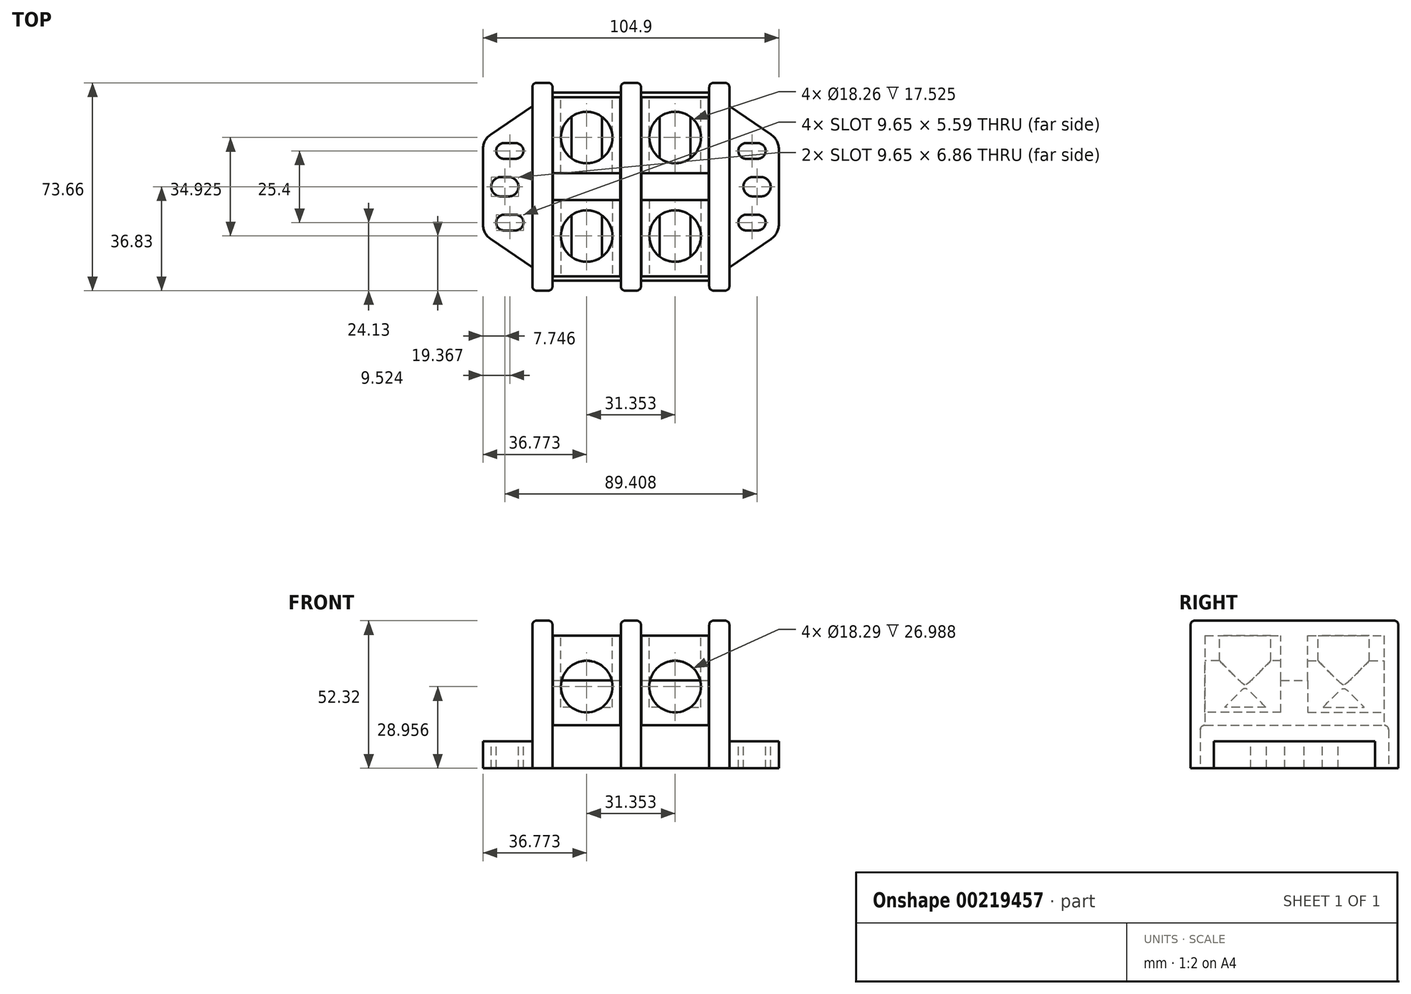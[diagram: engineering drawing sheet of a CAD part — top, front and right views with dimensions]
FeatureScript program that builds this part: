
annotation { "Feature Type Name" : "Feature", "Feature Type Description" : "" }
export const myFeature = defineFeature(function(context is Context, id is Id, definition is map)
    precondition{}
    {
        {
            var Q0;
            Q0=qCreatedBy(makeId("Top.planeOp"),FACE);
            var sketch = newSketch(context, id + "F0", { "sketchPlane" : qUnion([Q0])});
            skLineSegment(sketch, "E0.bottom", {"start": v(-3.57, -36.83) * mm, "end": v(3.57, -36.83) * mm});
            skLineSegment(sketch, "E0.top", {"start": v(-3.57, 36.83) * mm, "end": v(3.57, 36.83) * mm});
            skLineSegment(sketch, "E0.left", {"start": v(-3.57, -36.83) * mm, "end": v(-3.57, 36.83) * mm});
            skLineSegment(sketch, "E0.right", {"start": v(3.57, -36.83) * mm, "end": v(3.57, 36.83) * mm});
            skPoint(sketch, "E0.middle", {"position": v(0, 0) * mm});
            skLineSegment(sketch, "E1.bottom", {"start": v(-27.78, -36.83) * mm, "end": v(-34.93, -36.83) * mm});
            skLineSegment(sketch, "E1.top", {"start": v(-27.78, 36.83) * mm, "end": v(-34.93, 36.83) * mm});
            skLineSegment(sketch, "E1.left", {"start": v(-27.78, -36.83) * mm, "end": v(-27.78, 36.83) * mm});
            skLineSegment(sketch, "E1.right", {"start": v(-34.93, -36.83) * mm, "end": v(-34.93, 36.83) * mm});
            skPoint(sketch, "E1.middle", {"position": v(-31.35, 0) * mm});
            skLineSegment(sketch, "E2.bottom", {"start": v(27.78, -36.83) * mm, "end": v(34.93, -36.83) * mm});
            skLineSegment(sketch, "E2.top", {"start": v(27.78, 36.83) * mm, "end": v(34.93, 36.83) * mm});
            skLineSegment(sketch, "E2.left", {"start": v(27.78, -36.83) * mm, "end": v(27.78, 36.83) * mm});
            skLineSegment(sketch, "E2.right", {"start": v(34.93, -36.83) * mm, "end": v(34.93, 36.83) * mm});
            skPoint(sketch, "E2.middle", {"position": v(31.35, 0) * mm});
            skSolve(sketch);
        }
        {
            var Q0;
            Q0=qSketchRegion(id+"F0",true);
            extrude(context, id + "F1", {"entities" : qUnion([Q0]), "depth" : 52.32 * mm});
        }
        {
            var Q0;
            Q0=qCreatedBy(makeId("Top.planeOp"),FACE);
            var sketch = newSketch(context, id + "F2", { "sketchPlane" : qUnion([Q0])});
            skLineSegment(sketch, "E3.bottom", {"start": v(-27.78, -33.34) * mm, "end": v(27.78, -33.34) * mm});
            skLineSegment(sketch, "E3.top", {"start": v(-27.78, 33.34) * mm, "end": v(27.78, 33.34) * mm});
            skLineSegment(sketch, "E3.left", {"start": v(-27.78, -33.34) * mm, "end": v(-27.78, 33.34) * mm});
            skLineSegment(sketch, "E3.right", {"start": v(27.78, -33.34) * mm, "end": v(27.78, 33.34) * mm});
            skPoint(sketch, "E3.middle", {"position": v(0, 0) * mm});
            skSolve(sketch);
        }
        {
            var Q0;
            Q0=qSketchRegion(id+"F2",true);
            extrude(context, id + "F3", {"entities" : qUnion([Q0]), "depth" : 15.24 * mm});
        }
        {
            var Q0;
            Q0=qCreatedBy(makeId("Top.planeOp"),FACE);
            var sketch = newSketch(context, id + "F4", { "sketchPlane" : qUnion([Q0])});
            skLineSegment(sketch, "E4", {"start": v(-34.93, 28.58) * mm, "end": v(-52.45, 16.67) * mm});
            skLineSegment(sketch, "E5", {"start": v(-52.45, 16.67) * mm, "end": v(-52.45, -16.67) * mm});
            skLineSegment(sketch, "E6", {"start": v(-52.45, -16.67) * mm, "end": v(-34.93, -28.58) * mm});
            skLineSegment(sketch, "E7", {"start": v(-34.93, -28.58) * mm, "end": v(-34.93, 28.58) * mm});
            skSolve(sketch);
        }
        {
            var Q0;
            Q0=qSketchRegion(id+"F4",true);
            extrude(context, id + "F5", {"entities" : qUnion([Q0]), "operationType" : NewBodyOperationType.ADD, "depth" : 9.52 * mm});
        }
        {
            var Q0;
            Q0=makeQuery(id+"F1.opExtrude","SWEPT_EDGE",EDGE,{"disambiguationData":[OSD([sQuery(id+"F0.wireOp",EDGE,"E1.top"),sQuery(id+"F0.wireOp",EDGE,"E1.right")])]});
            var Q1;
            Q1=makeQuery(id+"F1.opExtrude","CAP_EDGE",EDGE,{"disambiguationData":[OSD([sQuery(id+"F0.wireOp",EDGE,"E1.right")])],"isStart":false});
            var Q2;
            Q2=makeQuery(id+"F1.opExtrude","SWEPT_EDGE",EDGE,{"disambiguationData":[OSD([sQuery(id+"F0.wireOp",EDGE,"E1.bottom"),sQuery(id+"F0.wireOp",EDGE,"E1.right")])]});
            var Q3;
            Q3=makeQuery(id+"F1.opExtrude","SWEPT_EDGE",EDGE,{"disambiguationData":[OSD([sQuery(id+"F0.wireOp",EDGE,"E1.bottom"),sQuery(id+"F0.wireOp",EDGE,"E1.left")])]});
            var Q4;
            Q4=makeQuery(id+"F1.opExtrude","CAP_EDGE",EDGE,{"disambiguationData":[OSD([sQuery(id+"F0.wireOp",EDGE,"E1.left")])],"isStart":false});
            var Q5;
            Q5=makeQuery(id+"F1.opExtrude","CAP_EDGE",EDGE,{"disambiguationData":[OSD([sQuery(id+"F0.wireOp",EDGE,"E1.bottom")])],"isStart":false});
            var Q6;
            Q6=makeQuery(id+"F1.opExtrude","CAP_EDGE",EDGE,{"disambiguationData":[OSD([sQuery(id+"F0.wireOp",EDGE,"E1.top")])],"isStart":false});
            var Q7;
            Q7=makeQuery(id+"F1.opExtrude","SWEPT_EDGE",EDGE,{"disambiguationData":[OSD([sQuery(id+"F0.wireOp",EDGE,"E1.top"),sQuery(id+"F0.wireOp",EDGE,"E1.left")])]});
            var Q8;
            Q8=makeQuery(id+"F3.opExtrude","CAP_EDGE",EDGE,{"disambiguationData":[OSD([sQuery(id+"F2.wireOp",EDGE,"E3.top")])],"isStart":false});
            var Q9;
            Q9=makeQuery(id+"F3.opExtrude","CAP_EDGE",EDGE,{"disambiguationData":[OSD([sQuery(id+"F2.wireOp",EDGE,"E3.bottom")])],"isStart":false});
            var Q10;
            Q10=makeQuery(id+"F1.opExtrude","SWEPT_EDGE",EDGE,{"disambiguationData":[OSD([sQuery(id+"F0.wireOp",EDGE,"E0.bottom"),sQuery(id+"F0.wireOp",EDGE,"E0.left")])]});
            var Q11;
            Q11=makeQuery(id+"F1.opExtrude","CAP_EDGE",EDGE,{"disambiguationData":[OSD([sQuery(id+"F0.wireOp",EDGE,"E0.left")])],"isStart":false});
            var Q12;
            Q12=makeQuery(id+"F1.opExtrude","CAP_EDGE",EDGE,{"disambiguationData":[OSD([sQuery(id+"F0.wireOp",EDGE,"E0.bottom")])],"isStart":false});
            var Q13;
            Q13=makeQuery(id+"F1.opExtrude","SWEPT_EDGE",EDGE,{"disambiguationData":[OSD([sQuery(id+"F0.wireOp",EDGE,"E0.bottom"),sQuery(id+"F0.wireOp",EDGE,"E0.right")])]});
            var Q14;
            Q14=makeQuery(id+"F1.opExtrude","CAP_EDGE",EDGE,{"disambiguationData":[OSD([sQuery(id+"F0.wireOp",EDGE,"E0.right")])],"isStart":false});
            var Q15;
            Q15=makeQuery(id+"F1.opExtrude","CAP_EDGE",EDGE,{"disambiguationData":[OSD([sQuery(id+"F0.wireOp",EDGE,"E0.top")])],"isStart":false});
            var Q16;
            Q16=makeQuery(id+"F1.opExtrude","SWEPT_EDGE",EDGE,{"disambiguationData":[OSD([sQuery(id+"F0.wireOp",EDGE,"E0.top"),sQuery(id+"F0.wireOp",EDGE,"E0.right")])]});
            var Q17;
            Q17=makeQuery(id+"F1.opExtrude","SWEPT_EDGE",EDGE,{"disambiguationData":[OSD([sQuery(id+"F0.wireOp",EDGE,"E0.top"),sQuery(id+"F0.wireOp",EDGE,"E0.left")])]});
            var Q18;
            Q18=makeQuery(id+"F1.opExtrude","SWEPT_EDGE",EDGE,{"disambiguationData":[OSD([sQuery(id+"F0.wireOp",EDGE,"E2.bottom"),sQuery(id+"F0.wireOp",EDGE,"E2.left")])]});
            var Q19;
            Q19=makeQuery(id+"F1.opExtrude","SWEPT_EDGE",EDGE,{"disambiguationData":[OSD([sQuery(id+"F0.wireOp",EDGE,"E2.bottom"),sQuery(id+"F0.wireOp",EDGE,"E2.right")])]});
            var Q20;
            Q20=makeQuery(id+"F1.opExtrude","CAP_EDGE",EDGE,{"disambiguationData":[OSD([sQuery(id+"F0.wireOp",EDGE,"E2.bottom")])],"isStart":false});
            var Q21;
            Q21=makeQuery(id+"F1.opExtrude","CAP_EDGE",EDGE,{"disambiguationData":[OSD([sQuery(id+"F0.wireOp",EDGE,"E2.left")])],"isStart":false});
            var Q22;
            Q22=makeQuery(id+"F1.opExtrude","CAP_EDGE",EDGE,{"disambiguationData":[OSD([sQuery(id+"F0.wireOp",EDGE,"E2.right")])],"isStart":false});
            var Q23;
            Q23=makeQuery(id+"F1.opExtrude","CAP_EDGE",EDGE,{"disambiguationData":[OSD([sQuery(id+"F0.wireOp",EDGE,"E2.top")])],"isStart":false});
            var Q24;
            Q24=makeQuery(id+"F1.opExtrude","SWEPT_EDGE",EDGE,{"disambiguationData":[OSD([sQuery(id+"F0.wireOp",EDGE,"E2.top"),sQuery(id+"F0.wireOp",EDGE,"E2.left")])]});
            var Q25;
            Q25=makeQuery(id+"F1.opExtrude","SWEPT_EDGE",EDGE,{"disambiguationData":[OSD([sQuery(id+"F0.wireOp",EDGE,"E2.top"),sQuery(id+"F0.wireOp",EDGE,"E2.right")])]});
            fillet(context, id + "F6", {"entities" : qUnion([Q0, Q1, Q2, Q3, Q4, Q5, Q6, Q7, Q8, Q9, Q10, Q11, Q12, Q13, Q14, Q15, Q16, Q17, Q18, Q19, Q20, Q21, Q22, Q23, Q24, Q25]), "radius" : 1.52 * mm, "tangentPropagation" : true});
        }
        {
            var Q0;
            Q0=qCreatedBy(makeId("Top.planeOp"),FACE);
            var sketch = newSketch(context, id + "F7", { "sketchPlane" : qUnion([Q0])});
            skLineSegment(sketch, "E8", {"start": v(34.93, 28.58) * mm, "end": v(52.45, 16.67) * mm});
            skLineSegment(sketch, "E9", {"start": v(52.45, 16.67) * mm, "end": v(52.45, -16.67) * mm});
            skLineSegment(sketch, "E10", {"start": v(52.45, -16.67) * mm, "end": v(34.93, -28.58) * mm});
            skLineSegment(sketch, "E11", {"start": v(34.93, -28.58) * mm, "end": v(34.93, 28.57) * mm});
            skSolve(sketch);
        }
        {
            var Q0;
            Q0=qSketchRegion(id+"F7",true);
            extrude(context, id + "F8", {"entities" : qUnion([Q0]), "operationType" : NewBodyOperationType.ADD, "depth" : 9.52 * mm});
        }
        {
            var Q0;
            Q0=makeQuery(id+"F5.opExtrude","CAP_FACE",FACE,{"disambiguationData":[OSD([sQuery(id+"F4.wireOp",EDGE,"E4"),sQuery(id+"F4.wireOp",EDGE,"E5"),sQuery(id+"F4.wireOp",EDGE,"E6"),sQuery(id+"F4.wireOp",EDGE,"E7")])],"isStart":false});
            var sketch = newSketch(context, id + "F9", { "sketchPlane" : qUnion([Q0])});
            skLineSegment(sketch, "E12.bottom", {"start": v(-40.9, 9.9) * mm, "end": v(-44.96, 9.9) * mm});
            skLineSegment(sketch, "E12.top", {"start": v(-40.9, 15.5) * mm, "end": v(-44.96, 15.5) * mm});
            skLineSegment(sketch, "E12.left", {"start": v(-40.9, 9.9) * mm, "end": v(-40.9, 15.5) * mm});
            skLineSegment(sketch, "E12.right", {"start": v(-44.96, 9.9) * mm, "end": v(-44.96, 15.5) * mm});
            skPoint(sketch, "E12.middle", {"position": v(-42.93, 12.7) * mm});
            skLineSegment(sketch, "E13.bottom", {"start": v(-43.3, -3.43) * mm, "end": v(-46.1, -3.43) * mm});
            skLineSegment(sketch, "E13.top", {"start": v(-43.3, 3.43) * mm, "end": v(-46.1, 3.43) * mm});
            skLineSegment(sketch, "E13.left", {"start": v(-43.3, -3.43) * mm, "end": v(-43.3, 3.43) * mm});
            skLineSegment(sketch, "E13.right", {"start": v(-46.1, -3.43) * mm, "end": v(-46.1, 3.43) * mm});
            skPoint(sketch, "E13.middle", {"position": v(-44.7, 0) * mm});
            skLineSegment(sketch, "E14.bottom", {"start": v(-40.9, -15.5) * mm, "end": v(-44.96, -15.5) * mm});
            skLineSegment(sketch, "E14.top", {"start": v(-40.9, -9.9) * mm, "end": v(-44.96, -9.9) * mm});
            skLineSegment(sketch, "E14.left", {"start": v(-40.9, -15.5) * mm, "end": v(-40.9, -9.9) * mm});
            skLineSegment(sketch, "E14.right", {"start": v(-44.96, -15.5) * mm, "end": v(-44.96, -9.9) * mm});
            skPoint(sketch, "E14.middle", {"position": v(-42.93, -12.7) * mm});
            skPoint(sketch, "E14.middle.positionSnap0", {"position": v(-42.93, 9.9) * mm});
            skPoint(sketch, "E14.centerSnap0", {"position": v(-42.93, 9.9) * mm});
            skArc(sketch, "E15", {"start": v(-44.96, 15.5) * mm, "mid": v(-47.75, 12.7) * mm, "end": v(-44.96, 9.9) * mm});
            skArc(sketch, "E16", {"start": v(-40.9, 9.9) * mm, "mid": v(-38.1, 12.7) * mm, "end": v(-40.9, 15.5) * mm});
            skArc(sketch, "E17", {"start": v(-46.1, 3.43) * mm, "mid": v(-49.53, 0) * mm, "end": v(-46.1, -3.43) * mm});
            skArc(sketch, "E18", {"start": v(-43.3, -3.43) * mm, "mid": v(-39.88, 0) * mm, "end": v(-43.3, 3.43) * mm});
            skArc(sketch, "E19", {"start": v(-44.96, -9.9) * mm, "mid": v(-47.75, -12.7) * mm, "end": v(-44.96, -15.5) * mm});
            skArc(sketch, "E20", {"start": v(-40.9, -15.5) * mm, "mid": v(-38.1, -12.7) * mm, "end": v(-40.9, -9.9) * mm});
            skSolve(sketch);
        }
        {
            var Q0;
            Q0=qSketchRegion(id+"F9",true);
            extrude(context, id + "F10", {"entities" : qUnion([Q0]), "operationType" : NewBodyOperationType.REMOVE, "oppositeDirection" : true, "depth" : 9.52 * mm});
        }
        {
            var Q0;
            Q0=makeQuery(id+"F8.opExtrude","CAP_FACE",FACE,{"disambiguationData":[OSD([sQuery(id+"F7.wireOp",EDGE,"E8"),sQuery(id+"F7.wireOp",EDGE,"E9"),sQuery(id+"F7.wireOp",EDGE,"E10"),sQuery(id+"F7.wireOp",EDGE,"E11")])],"isStart":false});
            var sketch = newSketch(context, id + "F11", { "sketchPlane" : qUnion([Q0])});
            skLineSegment(sketch, "E21.bottom", {"start": v(43.3, -3.43) * mm, "end": v(46.1, -3.43) * mm});
            skLineSegment(sketch, "E21.top", {"start": v(43.3, 3.43) * mm, "end": v(46.1, 3.43) * mm});
            skLineSegment(sketch, "E21.left", {"start": v(43.3, -3.43) * mm, "end": v(43.3, 3.43) * mm});
            skLineSegment(sketch, "E21.right", {"start": v(46.1, -3.43) * mm, "end": v(46.1, 3.43) * mm});
            skPoint(sketch, "E21.middle", {"position": v(44.7, 0) * mm});
            skLineSegment(sketch, "E22.bottom", {"start": v(44.96, 9.9) * mm, "end": v(40.9, 9.9) * mm});
            skLineSegment(sketch, "E22.top", {"start": v(44.96, 15.5) * mm, "end": v(40.9, 15.5) * mm});
            skLineSegment(sketch, "E22.left", {"start": v(44.96, 9.9) * mm, "end": v(44.96, 15.5) * mm});
            skLineSegment(sketch, "E22.right", {"start": v(40.9, 9.9) * mm, "end": v(40.9, 15.5) * mm});
            skPoint(sketch, "E22.middle", {"position": v(42.93, 12.7) * mm});
            skLineSegment(sketch, "E23.bottom", {"start": v(44.96, -15.5) * mm, "end": v(40.9, -15.5) * mm});
            skLineSegment(sketch, "E23.top", {"start": v(44.96, -9.9) * mm, "end": v(40.9, -9.9) * mm});
            skLineSegment(sketch, "E23.left", {"start": v(44.96, -15.5) * mm, "end": v(44.96, -9.9) * mm});
            skLineSegment(sketch, "E23.right", {"start": v(40.9, -15.5) * mm, "end": v(40.9, -9.9) * mm});
            skPoint(sketch, "E23.middle", {"position": v(42.93, -12.7) * mm});
            skArc(sketch, "E24", {"start": v(40.9, 15.5) * mm, "mid": v(38.1, 12.7) * mm, "end": v(40.9, 9.9) * mm});
            skArc(sketch, "E25", {"start": v(44.96, 9.9) * mm, "mid": v(47.75, 12.7) * mm, "end": v(44.96, 15.5) * mm});
            skArc(sketch, "E26", {"start": v(43.3, 3.43) * mm, "mid": v(39.88, 0) * mm, "end": v(43.3, -3.43) * mm});
            skArc(sketch, "E27", {"start": v(46.1, -3.43) * mm, "mid": v(49.53, 0) * mm, "end": v(46.1, 3.43) * mm});
            skArc(sketch, "E28", {"start": v(40.9, -9.9) * mm, "mid": v(38.1, -12.7) * mm, "end": v(40.9, -15.5) * mm});
            skArc(sketch, "E29", {"start": v(44.96, -15.5) * mm, "mid": v(47.75, -12.7) * mm, "end": v(44.96, -9.9) * mm});
            skSolve(sketch);
        }
        {
            var Q0;
            Q0=qSketchRegion(id+"F11",true);
            extrude(context, id + "F12", {"entities" : qUnion([Q0]), "operationType" : NewBodyOperationType.REMOVE, "oppositeDirection" : true, "depth" : 9.52 * mm});
        }
        {
            var Q0;
            Q0=makeQuery(id+"F5.opExtrude","SWEPT_EDGE",EDGE,{"disambiguationData":[OSD([sQuery(id+"F4.wireOp",EDGE,"E4"),sQuery(id+"F4.wireOp",EDGE,"E5")])]});
            var Q1;
            Q1=makeQuery(id+"F5.opExtrude","SWEPT_EDGE",EDGE,{"disambiguationData":[OSD([sQuery(id+"F4.wireOp",EDGE,"E5"),sQuery(id+"F4.wireOp",EDGE,"E6")])]});
            var Q2;
            Q2=makeQuery(id+"F8.opExtrude","SWEPT_EDGE",EDGE,{"disambiguationData":[OSD([sQuery(id+"F7.wireOp",EDGE,"E8"),sQuery(id+"F7.wireOp",EDGE,"E9")])]});
            var Q3;
            Q3=makeQuery(id+"F8.opExtrude","SWEPT_EDGE",EDGE,{"disambiguationData":[OSD([sQuery(id+"F7.wireOp",EDGE,"E9"),sQuery(id+"F7.wireOp",EDGE,"E10")])]});
            fillet(context, id + "F13", {"entities" : qUnion([Q0, Q1, Q2, Q3]), "radius" : 6.35 * mm, "tangentPropagation" : true});
        }
        {
            var Q0;
            Q0=makeQuery(id+"F1.opExtrude","SWEPT_BODY",BODY,{"disambiguationData":[OSD([sQuery(id+"F0.wireOp",EDGE,"E0.bottom"),sQuery(id+"F0.wireOp",EDGE,"E0.top"),sQuery(id+"F0.wireOp",EDGE,"E0.left"),sQuery(id+"F0.wireOp",EDGE,"E0.right")])]});
            var Q1;
            Q1=makeQuery(id+"F1.opExtrude","SWEPT_BODY",BODY,{"disambiguationData":[OSD([sQuery(id+"F0.wireOp",EDGE,"E1.bottom"),sQuery(id+"F0.wireOp",EDGE,"E1.top"),sQuery(id+"F0.wireOp",EDGE,"E1.left"),sQuery(id+"F0.wireOp",EDGE,"E1.right")])]});
            var Q2;
            Q2=makeQuery(id+"F1.opExtrude","SWEPT_BODY",BODY,{"disambiguationData":[OSD([sQuery(id+"F0.wireOp",EDGE,"E2.bottom"),sQuery(id+"F0.wireOp",EDGE,"E2.top"),sQuery(id+"F0.wireOp",EDGE,"E2.left"),sQuery(id+"F0.wireOp",EDGE,"E2.right")])]});
            var Q3;
            Q3=makeQuery(id+"F3.opExtrude","SWEPT_BODY",BODY,{"disambiguationData":[OSD([sQuery(id+"F2.wireOp",EDGE,"E3.bottom"),sQuery(id+"F2.wireOp",EDGE,"E3.top"),sQuery(id+"F2.wireOp",EDGE,"E3.left"),sQuery(id+"F2.wireOp",EDGE,"E3.right")])]});
            booleanBodies(context, id + "F14", {"operationType" : BooleanOperationType.UNION, "tools" : qUnion([Q0, Q1, Q2, Q3])});
        }
        {
            var Q0;
            {var subQ0=sQuery(id+"F2.wireOp",EDGE,"E3.top");var subQ1=sQuery(id+"F2.wireOp",EDGE,"E3.bottom");Q0=makeQuery(id+"F14.opBoolean","SPLIT",FACE,{"disambiguationData":[TD([makeQuery(id+"F1.opExtrude","SWEPT_FACE",FACE,{"disambiguationData":[OSD([sQuery(id+"F0.wireOp",EDGE,"E0.left")])]})])],"derivedFrom":makeQuery(id+"F3.opExtrude","CAP_FACE",FACE,{"disambiguationData":[OSD([subQ1,subQ0,sQuery(id+"F2.wireOp",EDGE,"E3.left"),sQuery(id+"F2.wireOp",EDGE,"E3.right")])],"isStart":false})});}
            var sketch = newSketch(context, id + "F15", { "sketchPlane" : qUnion([Q0])});
            skLineSegment(sketch, "E30.bottom", {"start": v(-27.58, -31.75) * mm, "end": v(-3.77, -31.75) * mm});
            skLineSegment(sketch, "E30.top", {"start": v(-27.58, 31.75) * mm, "end": v(-3.77, 31.75) * mm});
            skLineSegment(sketch, "E30.left", {"start": v(-27.58, -31.75) * mm, "end": v(-27.58, 31.75) * mm});
            skLineSegment(sketch, "E30.right", {"start": v(-3.77, -31.75) * mm, "end": v(-3.77, 31.75) * mm});
            skPoint(sketch, "E30.middle", {"position": v(-15.68, 0) * mm});
            skPoint(sketch, "E30.middle.positionSnap0", {"position": v(-3.57, 0) * mm});
            skPoint(sketch, "E30.centerSnap0", {"position": v(-3.57, 0) * mm});
            skSolve(sketch);
        }
        {
            var Q0;
            {var subQ0=sQuery(id+"F2.wireOp",EDGE,"E3.bottom");var subQ1=sQuery(id+"F2.wireOp",EDGE,"E3.top");Q0=makeQuery(id+"F14.opBoolean","SPLIT",FACE,{"disambiguationData":[TD([makeQuery(id+"F1.opExtrude","SWEPT_FACE",FACE,{"disambiguationData":[OSD([sQuery(id+"F0.wireOp",EDGE,"E0.right")])]})])],"derivedFrom":makeQuery(id+"F3.opExtrude","CAP_FACE",FACE,{"disambiguationData":[OSD([subQ0,subQ1,sQuery(id+"F2.wireOp",EDGE,"E3.left"),sQuery(id+"F2.wireOp",EDGE,"E3.right")])],"isStart":false})});}
            var sketch = newSketch(context, id + "F16", { "sketchPlane" : qUnion([Q0])});
            skLineSegment(sketch, "E31.bottom", {"start": v(3.77, -31.75) * mm, "end": v(27.58, -31.75) * mm});
            skLineSegment(sketch, "E31.top", {"start": v(3.77, 31.75) * mm, "end": v(27.58, 31.75) * mm});
            skLineSegment(sketch, "E31.left", {"start": v(3.77, -31.75) * mm, "end": v(3.77, 31.75) * mm});
            skLineSegment(sketch, "E31.right", {"start": v(27.58, -31.75) * mm, "end": v(27.58, 31.75) * mm});
            skPoint(sketch, "E31.middle", {"position": v(15.68, 0) * mm});
            skSolve(sketch);
        }
        {
            var Q0;
            Q0=qSketchRegion(id+"F15",true);
            var Q1;
            Q1=qSketchRegion(id+"F16",true);
            extrude(context, id + "F17", {"entities" : qUnion([Q0, Q1]), "depth" : 31.75 * mm});
        }
        {
            var Q0;
            Q0=makeQuery(id+"F17.opExtrude","CAP_FACE",FACE,{"disambiguationData":[OSD([sQuery(id+"F15.wireOp",EDGE,"E30.bottom"),sQuery(id+"F15.wireOp",EDGE,"E30.top"),sQuery(id+"F15.wireOp",EDGE,"E30.left"),sQuery(id+"F15.wireOp",EDGE,"E30.right")])],"isStart":false});
            var sketch = newSketch(context, id + "F18", { "sketchPlane" : qUnion([Q0])});
            skCircle(sketch, "E32", {"center": v(-15.68, 17.46) * mm, "radius": 9.13 * mm});
            skCircle(sketch, "E33", {"center": v(-15.68, -17.46) * mm, "radius": 9.13 * mm});
            skSolve(sketch);
        }
        {
            var Q0;
            Q0=qSketchRegion(id+"F18",true);
            extrude(context, id + "F19", {"entities" : qUnion([Q0]), "operationType" : NewBodyOperationType.REMOVE, "oppositeDirection" : true, "depth" : 25.4 * mm});
        }
        {
            var Q0;
            Q0=makeQuery(id+"F17.opExtrude","CAP_FACE",FACE,{"disambiguationData":[OSD([sQuery(id+"F16.wireOp",EDGE,"E31.bottom"),sQuery(id+"F16.wireOp",EDGE,"E31.top"),sQuery(id+"F16.wireOp",EDGE,"E31.left"),sQuery(id+"F16.wireOp",EDGE,"E31.right")])],"isStart":false});
            var sketch = newSketch(context, id + "F20", { "sketchPlane" : qUnion([Q0])});
            skCircle(sketch, "E34", {"center": v(15.68, 17.46) * mm, "radius": 9.13 * mm});
            skCircle(sketch, "E35", {"center": v(15.68, -17.46) * mm, "radius": 9.13 * mm});
            skSolve(sketch);
        }
        {
            var Q0;
            Q0=qSketchRegion(id+"F20",true);
            extrude(context, id + "F21", {"entities" : qUnion([Q0]), "operationType" : NewBodyOperationType.REMOVE, "oppositeDirection" : true, "depth" : 25.4 * mm});
        }
        {
            var Q0;
            Q0=makeQuery(id+"F17.opExtrude","CAP_FACE",FACE,{"disambiguationData":[OSD([sQuery(id+"F15.wireOp",EDGE,"E30.bottom"),sQuery(id+"F15.wireOp",EDGE,"E30.top"),sQuery(id+"F15.wireOp",EDGE,"E30.left"),sQuery(id+"F15.wireOp",EDGE,"E30.right")])],"isStart":false});
            var sketch = newSketch(context, id + "F22", { "sketchPlane" : qUnion([Q0])});
            skLineSegment(sketch, "E36.bottom", {"start": v(-27.58, 4.76) * mm, "end": v(-3.77, 4.76) * mm});
            skLineSegment(sketch, "E36.top", {"start": v(-27.58, -4.76) * mm, "end": v(-3.77, -4.76) * mm});
            skLineSegment(sketch, "E36.left", {"start": v(-27.58, 4.76) * mm, "end": v(-27.58, -4.76) * mm});
            skLineSegment(sketch, "E36.right", {"start": v(-3.77, 4.76) * mm, "end": v(-3.77, -4.76) * mm});
            skSolve(sketch);
        }
        {
            var Q0;
            Q0=makeQuery(id+"F22.imprint","IMPRINT",FACE,{"disambiguationData":[TD([[makeQuery(id+"F22.imprint","IMPRINT",EDGE,{"derivedFrom":sQuery(id+"F22.wireOp",EDGE,"E36.bottom")}),-1.0]])]});
            extrude(context, id + "F23", {"entities" : qUnion([Q0]), "operationType" : NewBodyOperationType.REMOVE, "oppositeDirection" : true, "depth" : 15.88 * mm});
        }
        {
            var Q0;
            Q0=makeQuery(id+"F17.opExtrude","CAP_FACE",FACE,{"disambiguationData":[OSD([sQuery(id+"F16.wireOp",EDGE,"E31.bottom"),sQuery(id+"F16.wireOp",EDGE,"E31.top"),sQuery(id+"F16.wireOp",EDGE,"E31.left"),sQuery(id+"F16.wireOp",EDGE,"E31.right")])],"isStart":false});
            var sketch = newSketch(context, id + "F24", { "sketchPlane" : qUnion([Q0])});
            skLineSegment(sketch, "E37.bottom", {"start": v(3.77, 4.76) * mm, "end": v(27.58, 4.76) * mm});
            skLineSegment(sketch, "E37.top", {"start": v(3.77, -4.76) * mm, "end": v(27.58, -4.76) * mm});
            skLineSegment(sketch, "E37.left", {"start": v(3.77, 4.76) * mm, "end": v(3.77, -4.76) * mm});
            skLineSegment(sketch, "E37.right", {"start": v(27.58, 4.76) * mm, "end": v(27.58, -4.76) * mm});
            skSolve(sketch);
        }
        {
            var Q0;
            Q0=qSketchRegion(id+"F24",true);
            extrude(context, id + "F25", {"entities" : qUnion([Q0]), "operationType" : NewBodyOperationType.REMOVE, "oppositeDirection" : true, "depth" : 15.88 * mm});
        }
        {
            var Q0;
            Q0=makeQuery(id+"F17.opExtrude","SWEPT_FACE",FACE,{"disambiguationData":[OSD([sQuery(id+"F15.wireOp",EDGE,"E30.bottom")])]});
            var sketch = newSketch(context, id + "F26", { "sketchPlane" : qUnion([Q0])});
            skCircle(sketch, "E38", {"center": v(-15.68, 28.96) * mm, "radius": 9.14 * mm});
            skSolve(sketch);
        }
        {
            var Q0;
            Q0=qSketchRegion(id+"F26",true);
            extrude(context, id + "F27", {"entities" : qUnion([Q0]), "operationType" : NewBodyOperationType.REMOVE, "oppositeDirection" : true, "depth" : 26.99 * mm});
        }
        {
            var Q0;
            Q0=makeQuery(id+"F17.opExtrude","SWEPT_FACE",FACE,{"disambiguationData":[OSD([sQuery(id+"F16.wireOp",EDGE,"E31.bottom")])]});
            var sketch = newSketch(context, id + "F28", { "sketchPlane" : qUnion([Q0])});
            skCircle(sketch, "E39", {"center": v(15.68, 28.96) * mm, "radius": 9.14 * mm});
            skPoint(sketch, "E39.centerSnap0", {"position": v(15.68, 15.24) * mm});
            skSolve(sketch);
        }
        {
            var Q0;
            Q0=qSketchRegion(id+"F28",true);
            extrude(context, id + "F29", {"entities" : qUnion([Q0]), "operationType" : NewBodyOperationType.REMOVE, "oppositeDirection" : true, "depth" : 26.99 * mm});
        }
        {
            var Q0;
            Q0=makeQuery(id+"F17.opExtrude","SWEPT_FACE",FACE,{"disambiguationData":[OSD([sQuery(id+"F16.wireOp",EDGE,"E31.top")])]});
            var sketch = newSketch(context, id + "F30", { "sketchPlane" : qUnion([Q0])});
            skCircle(sketch, "E40", {"center": v(-15.68, 28.96) * mm, "radius": 9.14 * mm});
            skPoint(sketch, "E40.centerSnap0", {"position": v(-15.68, 47) * mm});
            skSolve(sketch);
        }
        {
            var Q0;
            Q0=makeQuery(id+"F17.opExtrude","SWEPT_FACE",FACE,{"disambiguationData":[OSD([sQuery(id+"F15.wireOp",EDGE,"E30.top")])]});
            var sketch = newSketch(context, id + "F31", { "sketchPlane" : qUnion([Q0])});
            skCircle(sketch, "E41", {"center": v(15.68, 28.96) * mm, "radius": 9.14 * mm});
            skPoint(sketch, "E41.centerSnap0", {"position": v(15.68, 47) * mm});
            skSolve(sketch);
        }
        {
            var Q0;
            Q0=qSketchRegion(id+"F30",true);
            extrude(context, id + "F32", {"entities" : qUnion([Q0]), "operationType" : NewBodyOperationType.REMOVE, "oppositeDirection" : true, "depth" : 26.99 * mm});
        }
        {
            var Q0;
            Q0=qSketchRegion(id+"F31",true);
            extrude(context, id + "F33", {"entities" : qUnion([Q0]), "operationType" : NewBodyOperationType.REMOVE, "oppositeDirection" : true, "depth" : 26.99 * mm});
        }
    });
